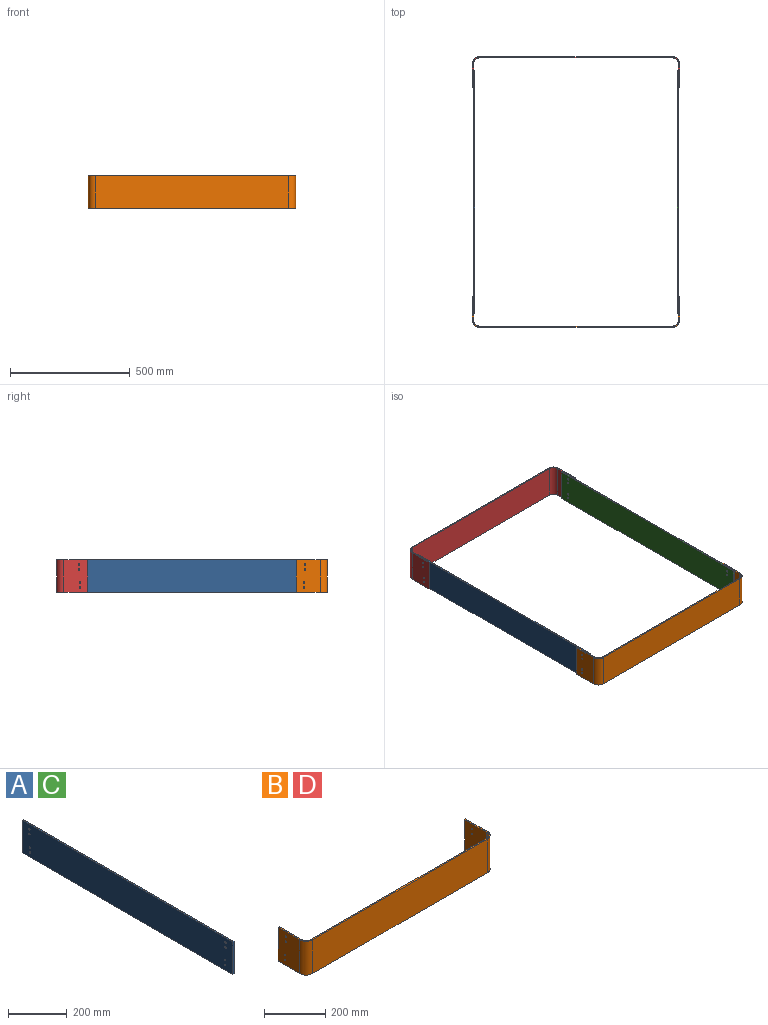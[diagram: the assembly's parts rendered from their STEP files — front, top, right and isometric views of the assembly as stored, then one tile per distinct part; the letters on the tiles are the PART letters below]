
ASSEMBLY  parts=4 mates=3
PART A: 14 faces, bbox 5x1012x135 mm
  f0: plane 135x5mm, normal (0,1,0), area 675mm2, adj f1,f10,f12,f13
  f1: plane 1011.97x5mm, normal (0,0,-1), area 5059.9mm2, adj f0,f2,f12,f13
  f2: plane 135x5mm, normal (0,-1,0), area 675mm2, adj f1,f10,f12,f13
  f3: cylinder r=3mm len=6mm, axis (1,0,0), area 94.2mm2, adj f12,f13
  f4: cylinder r=3mm len=6mm, axis (1,0,0), area 94.2mm2, adj f12,f13
  f5: cylinder r=3mm len=6mm, axis (1,0,0), area 94.2mm2, adj f12,f13
  f6: cylinder r=3mm len=6mm, axis (1,0,0), area 94.2mm2, adj f12,f13
  f7: cylinder r=3mm len=6mm, axis (1,0,0), area 94.2mm2, adj f12,f13
  f8: cylinder r=3mm len=6mm, axis (1,0,0), area 94.2mm2, adj f12,f13
  f9: cylinder r=3mm len=6mm, axis (1,0,0), area 94.2mm2, adj f12,f13
  f10: plane 1011.97x5mm, normal (0,0,1), area 5059.9mm2, adj f0,f2,f12,f13
  f11: cylinder r=3mm len=6mm, axis (1,0,0), area 94.2mm2, adj f12,f13
  f12: plane 1011.97x135mm, normal (-1,0,0), area 136389.9mm2, adj f0,f1,f2,f3,f4,f5,f6,f7
  f13: plane 1011.97x135mm, normal (1,0,0), area 136389.9mm2, adj f0,f1,f2,f3,f4,f5,f6,f7
PART B: 22 faces, bbox 865x130x135 mm
  f0: cylinder r=25mm len=135mm, axis (0,0,-1), area 5301.4mm2, adj f1,f11,f12,f13
  f1: plane 135x100mm, normal (1,0,0), area 13386.9mm2, adj f0,f2,f12,f13,f18,f19,f20,f21
  f2: plane 135x5mm, normal (0,1,0), area 675mm2, adj f1,f3,f12,f13
  f3: plane 135x100mm, normal (-1,0,0), area 13386.9mm2, adj f2,f4,f12,f13,f18,f19,f20,f21
  f4: cylinder r=30mm len=135mm, axis (0,0,-1), area 6361.7mm2, adj f3,f5,f12,f13
  f5: plane 805x135mm, normal (0,-1,0), area 108675mm2, adj f4,f6,f12,f13
  f6: cylinder r=30mm len=135mm, axis (0,0,-1), area 6361.7mm2, adj f5,f7,f12,f13
  f7: plane 135x100mm, normal (1,0,0), area 13386.9mm2, adj f6,f8,f12,f13,f14,f15,f16,f17
  f8: plane 135x5mm, normal (0,1,0), area 675mm2, adj f7,f9,f12,f13
  f9: plane 135x100mm, normal (-1,0,0), area 13386.9mm2, adj f8,f10,f12,f13,f14,f15,f16,f17
  f10: cylinder r=25mm len=135mm, axis (0,0,-1), area 5301.4mm2, adj f9,f11,f12,f13
  f11: plane 805x135mm, normal (0,1,0), area 108675mm2, adj f0,f10,f12,f13
  f12: plane 865x130mm, normal (0,0,1), area 5457mm2, adj f0,f1,f2,f3,f4,f5,f6,f7
  f13: plane 865x130mm, normal (0,0,-1), area 5457mm2, adj f0,f1,f2,f3,f4,f5,f6,f7
  f14: cylinder r=3mm len=6mm, axis (-1,0,0), area 94.2mm2, adj f7,f9
  f15: cylinder r=3mm len=6mm, axis (-1,0,0), area 94.2mm2, adj f7,f9
  f16: cylinder r=3mm len=6mm, axis (-1,0,0), area 94.2mm2, adj f7,f9
  f17: cylinder r=3mm len=6mm, axis (-1,0,0), area 94.2mm2, adj f7,f9
  f18: cylinder r=3mm len=6mm, axis (-1,0,0), area 94.2mm2, adj f1,f3
  f19: cylinder r=3mm len=6mm, axis (-1,0,0), area 94.2mm2, adj f1,f3
  f20: cylinder r=3mm len=6mm, axis (-1,0,0), area 94.2mm2, adj f1,f3
  f21: cylinder r=3mm len=6mm, axis (-1,0,0), area 94.2mm2, adj f1,f3
PART C: same geometry as A
PART D: same geometry as B
PLACE A rot(axis=(0,0,1),180deg) t=(335.22,366.67,531.95)mm
PLACE B t=(414.52,-342.87,531.95)mm
PLACE C t=(414.52,-342.87,531.95)mm
PLACE D rot(axis=(0,0,1),180deg) t=(335.22,366.67,531.95)mm
MATE planar B.f13 <-> A.f1  axis (0,0,-1) through (374.87,-535.61,531.95)mm
MATE planar A.f0 <-> C.f2  axis (0,-1,0) through (-50.13,-494.09,599.45)mm
MATE planar C.f7 <-> D.f1  axis (1,0,0) through (802.37,478.83,551.95)mm
